# Revit family: РОСМА_ТермометрКоррозионностЭлектроконтПриставкойУниверсПрисоед
name_source: partatom
category: Арматура трубопроводов
revit_build: Autodesk Revit 2018 (Build: 20180423_1000(x64)
units: mm (PartAtom-declared; Revit-internal decimal feet)

## family parameters
Всегда вертикально = Да
На основе рабочей плоскости = Нет
Общий = Нет
При загрузке вырезать с полостями = Нет
Размер круглого соединителя = Использовать диаметр
Тип детали = Вставляется

## types (1)
- 54
    ADSK_Единица измерения = шт.
    ADSK_Количество = 1
    C = 43 мм
    D = 100 мм
    D1 = 101 мм
    D2 = 99 мм
    D3 = 10 мм
    DN = 15.00 мм
    Dgol = 18 мм
    G = 20 мм
    L1 = 66 мм
    R1 шкала = 36 мм
    R2 шкала = 35 мм
    R_Logo = 20 мм
    Rg1 = 16 мм
    Rg2 = 20 мм
    S = 27 мм
    S1 = 22 мм
    Table = спец_коррозионностойкий с электроконтактной приставкой (универсальное присоединение)
    URL = https://rosma.spb.ru
    b = 87 мм
    b-e = 33 мм
    b1 = 65 мм
    e = 54 мм
    f = 0 мм
    h_rezba = 15 мм
    Группа модели = Оборудование
    Длина стрелки = 40 мм
    Длина02 = ᅠ : 64мм
    Длина03 = ᅠ : 100мм
    Длина04 = ᅠ : 150мм
    Длина05 = ᅠ : 200мм
    Длина06 = ᅠ : 250мм
    Длина07 = ᅠ : 300мм
    Изготовитель = ЗАО "РОСМА"
    Исполнение = 54
    Класс точности = 1,5
    Климатическое исполнение = Группа Д2 по ГОСТ Р 52931; климатическое исполнение УХЛ категории 1.1 по ГОСТ 15150
    Код IP = IP65
    Межповерочный интервал = 3 года
    Описание = Тип БТ, серия 220. Коррозионностойкий термометр с электроконтактной приставкой и универсальным присоединением (поворотно-откидным корпусом) с резьбой на штоке. Биметаллический термометр, устойчивый к воздействию агрессивных измеряемых сред; предназначен для управления внешними электрическими цепями в схемах сигнализации, автоматики и блокировки технологических процессов.
    Температура01 = ‎ : -30...+50°С
    Температура02 = ‎ : 0...+60°С
    Температура03 = ‎ : 0...+100°С
    Температура04 = ‎ : 0...+120°С
    Температура05 = ‎ : 0...+160°С
    Температура06 = ‎ : 0...+250°С
    Температура07 = ‎ : 0...+300°С
    Температура08 = ‎ : 0...+350°С
    Температура09 = ‎ : 0...+450°С
    Техническая документация = ТУ 4211-001-4719015564-2008
    лого_задн_стенка = Нет
